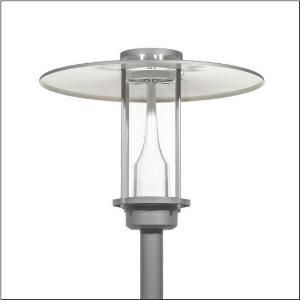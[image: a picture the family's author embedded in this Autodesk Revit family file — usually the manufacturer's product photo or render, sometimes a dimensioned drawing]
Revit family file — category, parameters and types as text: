
# Revit family: city-light_plus_iq___st1_2a_5xa5275kf14hp_140d
name_source: partatom
category: Lighting Fixtures
units: mm (PartAtom-declared; Revit-internal decimal feet)

## family parameters
Cut with Voids When Loaded = No
Host = Face
Light Source = No
Part Type = Normal
Room Calculation Point = No
Round Connector Dimension = Use Diameter
Shared = No

## types (1)
- --- (1 x LED, 4710 lm, 33.6 W, 4000K)
    Apparent Load = 34 VA
    CIE Flux Codes = 22 60 93 97 100
    Color Rendering = 70
    Color Temperature = 4000K
    Default Elevation = 1800 mm
    Description = City-Light Plus iQ, mast luminaire, Module 540 iQ-SR, primary light control with 3 zone facetted reflector, of plastic, silver coated, highly specular, structured, primary optical cover: cover, of PMMA, transparent, light distribution: ST1.2a, light emission: direct distribution, primary light characteristic: asymmetric, installation type: post-top, LED, High Power LED, rated luminous flux: 4.710lm, luminous efficacy: 140lm/W, light colour: 740, colour temperature: 4000K, control gear: ECG iQ, control: pre-setting: logarithmic dimming characteristic, Street-Remote, Auto-Match, Temp-Guard, Lumen-Switch, Night-Set, Smart-Wire, Light-Fading, Desk-Remote (wireless, voltage-free reading and setting of iQ features in the workshop via application-optimized NFC function/RFID function), optimised constant luminous flux control (CLO 2.0), with terminal, 6-pole, max. 2.5mm², mains connection: 230..240V, AC, 50/60Hz, start of lifetime: 34W, end of service life: 36W, reduction: 15W, luminaire housing, upper part, of glass-fibre reinforced polyester, coated, Siteco® metallic grey (DB 702S), diameter: 750mm, height: 590mm, spigot size: d x l = 76 x 70mm (post-top) | with reducer (optional accessory) 60 x 70mm, post-top mast mounting element, of diecast aluminium, coated, Siteco® metallic grey (DB 702S), Module 540 iQ-SR, traffic white (RAL 9016), equipment: Power, protection rating (complete): IP65, insulation class (complete): insulation class II (safety insulation), certification: CE, ENEC, VDE, packaging unit: 1 piece

Light Distribution: ST1.2a
    Height = 590 mm
    Lamp = 1 x LED
    Lamp Light Flux = 4710 lm
    Lamp Power = 33.6 W
    Lamp count = 1
    Length = 750 mm
    Luminous efficacy = 140 lm/W
    Manufacturer = Siteco
    ModVariant = No
    Model = 5XA5275KF14HP
    Number of Poles = 1
    OnlyDefault = Yes
    Power Factor = 1
    Product Name = City-Light Plus iQ | ST1.2a
    Product group = mast luminaire | pylon top
    ProductGroupID = 6100
    Protection Class = Protection class II
    Protection Degree = IP 65
    RLX_Detail_Level = 1
    RLX_Emergency_Light_Flux = 0 lm
    RLX_Emergency_Type = 0
    RLX_Emergency_Type_DB = No
    RlxData = <blob elided: 52557 chars, md5=0911582b>
    Socket = socket
    Standby Power = 0 W
    System Light Flux = 4710 lm
    System Power = 34 W
    Type Comments = factory setting: luminous flux: 100 % | dim-lin: 254 | 695 mA
    Type Image = l_1006456.jpg
    URL = http://relux.com
    VarID = @adj_166495
    Voltage = 0 V
    Weight = 0.00 kg
    Width = 0 mm  [stored 0 ft]

note: [stored X ft] marks values corroborated as IEEE doubles in the binary element streams (Revit-internal decimal feet)

## geometry (parser evidence)
native form markers: Blend x4, Sweep x13
no freeform markers — native parametric forms only
